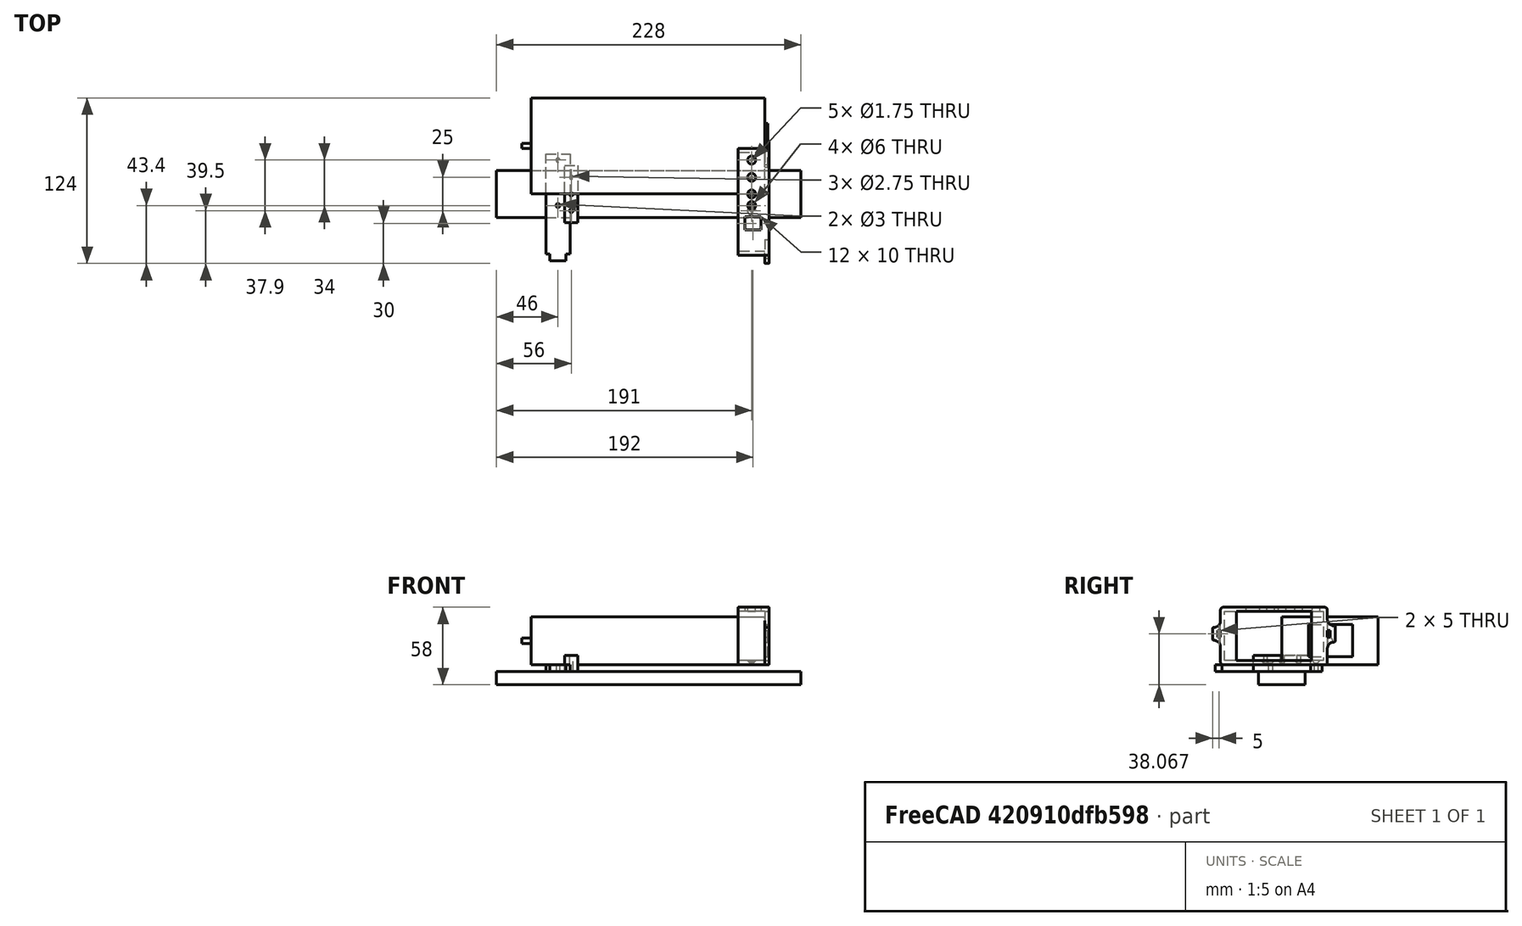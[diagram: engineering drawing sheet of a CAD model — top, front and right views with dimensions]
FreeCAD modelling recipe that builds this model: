
FCSTD DOCUMENT  (FreeCAD 0.18R)
Label: Powerbrick-Shoes
License: CreativeCommons Attribution
LicenseURL: http://creativecommons.org/licenses/by/4.0/
objects: Sketcher::SketchObject×6, Part::Box×4, PartDesign::Pad×4, PartDesign::Body×3, App::Part×2, Mesh::Feature×2, Part::Cylinder×1, Part::MultiFuse×1, PartDesign::Pocket×1, PartDesign::Hole×1, Part::Mirroring×1
note: 28 computed .brp shape members not serialized (recipe doc carries the construction recipe); baked Part::Feature solids carry a one-line shape summary decoded from their .brp

FEATURE [Part::Box] Box  label="Powerbrick-mw-gst160a"
  AttacherType = Attacher::AttachEngine3D
  Height = 36
  Length = 175
  Width = 72
FEATURE [Sketcher::SketchObject] Sketch
  MapMode = 5
  Support = -> [XY_Plane]
  sketch-geometry (10):
    g0: LineSegment StartX=-9 StartY=30 StartZ=0 EndX=9 EndY=30 EndZ=0
    g1: LineSegment StartX=9 StartY=30 StartZ=0 EndX=9 EndY=-45 EndZ=0
    g2: LineSegment StartX=-9 StartY=-45 StartZ=0 EndX=-9 EndY=30 EndZ=0
    g3: LineSegment StartX=-9 StartY=-45 StartZ=0 EndX=-6 EndY=-45 EndZ=0
    g4: LineSegment StartX=6 StartY=-45 StartZ=0 EndX=9 EndY=-45 EndZ=0
    g5: Circle CenterX=0 CenterY=25.4 CenterZ=0 NormalX=0 NormalY=0 NormalZ=1 AngleXU=0 Radius=1.5
    g6: Circle CenterX=0 CenterY=-8.6 CenterZ=0 NormalX=0 NormalY=0 NormalZ=1 AngleXU=0 Radius=1.5
    g7: LineSegment StartX=6 StartY=-45 StartZ=0 EndX=6 EndY=-50 EndZ=0
    g8: LineSegment StartX=6 StartY=-50 StartZ=0 EndX=-6 EndY=-50 EndZ=0
    g9: LineSegment StartX=-6 StartY=-50 StartZ=0 EndX=-6 EndY=-45 EndZ=0
  constraints (29):
    c: Coincident(g0,g1)
    c: Coincident(g2,g0)
    c: Vertical(g1)
    c: Vertical(g2)
    c: Coincident(g1,g4)
    c: Coincident(g2,g3)
    c: Horizontal(g3)
    c: Horizontal(g4)
    c: Equal(g2,g1)
    c: Symmetric(g0,g0,g-2)
    c: PointOnObject(g5,g-2)
    c: PointOnObject(g6,g-2)
    c: Radius(g5) = 1.5
    c: Equal(g5,g6)
    c: DistanceX(g0,g0) = 18
    c: DistanceY(g2,g2) = 75
    c: Coincident(g7,g8)
    c: Coincident(g8,g9)
    c: Coincident(g4,g7)
    c: Coincident(g9,g3)
    c: Vertical(g7)
    c: Vertical(g9)
    c: Horizontal(g8)
    c: Equal(g4,g3)
    c: DistanceX(g8,g8) = 12
    c: DistanceY(g7,g7) = 5
    c: DistanceY(g2,g-1) = 45
    c: DistanceY(g6,g-1) = 8.6
    c: DistanceY(g-1,g5) = 25.4
FEATURE [PartDesign::Pad] Pad
  Length = 5
  Length2 = 100
  Profile = -> Sketch
  Type = 0
FEATURE [PartDesign::Body] Body  label="APRA-Norm-Hutschienenklammer-442-311-35"
  Group = -> [Sketch,Pad]
  Origin = -> Origin
  Placement = pos=(20,0,-5) rot=(0,0,1;0rad)
  Tip = -> Pad
FEATURE [Part::Box] Box001  label="DIN Rail"
  AttacherType = Attacher::AttachEngine3D
  Height = 10
  Length = 228
  Placement = pos=(-26,-17.5,-15) rot=(0,0,1;0rad)
  Width = 35
FEATURE [Sketcher::SketchObject] Sketch001
  MapMode = 5
  Support = -> [XY_Plane001]
  sketch-geometry (7):
    g0: LineSegment StartX=-5 StartY=21.5 StartZ=0 EndX=5 EndY=21.5 EndZ=0
    g1: LineSegment StartX=5 StartY=21.5 StartZ=0 EndX=5 EndY=-21.5 EndZ=0
    g2: LineSegment StartX=5 StartY=-21.5 StartZ=0 EndX=-5 EndY=-21.5 EndZ=0
    g3: LineSegment StartX=-5 StartY=-21.5 StartZ=0 EndX=-5 EndY=21.5 EndZ=0
    g4: Circle CenterX=0 CenterY=12.5 CenterZ=0 NormalX=0 NormalY=0 NormalZ=1 AngleXU=0 Radius=1.375
    g5: Circle CenterX=0 CenterY=0 CenterZ=0 NormalX=0 NormalY=0 NormalZ=1 AngleXU=0 Radius=1.375
    g6: Circle CenterX=0 CenterY=-12.5 CenterZ=0 NormalX=0 NormalY=0 NormalZ=1 AngleXU=0 Radius=1.375
  constraints (17):
    c: Coincident(g0,g1)
    c: Coincident(g1,g2)
    c: Coincident(g2,g3)
    c: Coincident(g3,g0)
    c: Horizontal(g2)
    c: Vertical(g1)
    c: Symmetric(g0,g0,g-2)
    c: DistanceX(g0,g0) = 10
    c: DistanceY(g3,g3) = 43
    c: Symmetric(g2,g0,g-1)
    c: PointOnObject(g6,g-2)
    c: Coincident(g-1,g5)
    c: Symmetric(g6,g4,g-1)
    c: DistanceY(g6,g4) = 25
    c: Radius(g4) = 1.375
    c: Equal(g4,g5)
    c: Equal(g4,g6)
FEATURE [PartDesign::Pad] Pad001
  Length = 12
  Length2 = 100
  Profile = -> Sketch001
  Type = 0
FEATURE [PartDesign::Body] Body001  label="China-Clamp-DIN-Rail"
  Group = -> [Sketch001,Pad001]
  Origin = -> Origin001
  Placement = pos=(30,0,-5) rot=(0,0,1;0rad)
  Tip = -> Pad001
FEATURE [Sketcher::SketchObject] Sketch002
  MapMode = 5
  Placement = pos=(0,0,0) rot=(0.57735,0.57735,0.57735;2.0944rad)
  Support = -> [YZ_Plane003]
  sketch-geometry (12):
    g0: LineSegment StartX=-43 StartY=3 StartZ=0 EndX=-43 EndY=40 EndZ=0
    g1: LineSegment StartX=-43 StartY=40 StartZ=0 EndX=31 EndY=40 EndZ=0
    g2: LineSegment StartX=31 StartY=40 StartZ=0 EndX=31 EndY=3 EndZ=0
    g3: LineSegment StartX=31 StartY=3 StartZ=0 EndX=-43 EndY=3 EndZ=0
    g4: LineSegment StartX=-46 StartY=2 StartZ=0 EndX=-46 EndY=41 EndZ=0
    g5: ArcOfCircle CenterX=-44 CenterY=41 CenterZ=0 NormalX=0 NormalY=0 NormalZ=1 AngleXU=0 Radius=2 StartAngle=1.5708 EndAngle=3.14159
    g6: LineSegment StartX=-44 StartY=43 StartZ=0 EndX=32 EndY=43 EndZ=0
    g7: ArcOfCircle CenterX=32 CenterY=41 CenterZ=0 NormalX=0 NormalY=0 NormalZ=1 AngleXU=0 Radius=2 StartAngle=1.6e-15 EndAngle=1.5708
    g8: LineSegment StartX=34 StartY=41 StartZ=0 EndX=34 EndY=2 EndZ=0
    g9: ArcOfCircle CenterX=32 CenterY=2 CenterZ=0 NormalX=0 NormalY=0 NormalZ=1 AngleXU=0 Radius=2 StartAngle=4.71239 EndAngle=6.28319
    g10: LineSegment StartX=32 StartY=0 StartZ=0 EndX=-44 EndY=0 EndZ=0
    g11: ArcOfCircle CenterX=-44 CenterY=2 CenterZ=0 NormalX=0 NormalY=0 NormalZ=1 AngleXU=0 Radius=2 StartAngle=3.14159 EndAngle=4.71239
  constraints (32):
    c: Coincident(g0,g1)
    c: Coincident(g1,g2)
    c: Coincident(g2,g3)
    c: Coincident(g3,g0)
    c: Tangent(g4,g5) = 1.5708
    c: Tangent(g5,g6) = 1.5708
    c: Tangent(g6,g7) = 1.5708
    c: Tangent(g7,g8) = 1.5708
    c: Tangent(g8,g9) = 1.5708
    c: Horizontal(g6)
    c: Horizontal(g1)
    c: Horizontal(g3)
    c: Vertical(g8)
    c: Vertical(g0)
    c: Vertical(g2)
    c: Vertical(g4)
    c: Tangent(g4,g11) = 1.5708
    c: Tangent(g10,g11) = 1.5708
    c: Tangent(g9,g10) = 1.5708
    c: PointOnObject(g10,g-1)
    c: Horizontal(g10)
    c: DistanceY(g-1,g2) = 3
    c: DistanceX(g3,g3) = 74
    c: DistanceY(g2,g2) = 37
    c: DistanceY(g1,g6) = 3
    c: DistanceX(g1,g7) = 3
    c: DistanceX(g4,g0) = 3
    c: Radius(g7) = 2
    c: Equal(g7,g5)
    c: Equal(g7,g11)
    c: Equal(g7,g9)
    c: DistanceX(g-1,g2) = 31
FEATURE [PartDesign::Pad] Pad002
  Length = 20
  Length2 = 100
  Placement = pos=(0,0,0) rot=(0.57735,0.57735,0.57735;2.0944rad)
  Profile = -> Sketch002
  Type = 0
FEATURE [Part::Box] Box002  label="LED"
  AttacherType = Attacher::AttachEngine3D
  Height = 10
  Length = 7
  Placement = pos=(5,18,26) rot=(0,0,1;0rad)
  Width = 4
FEATURE [Part::Cylinder] Cylinder  label="24V Cable"
  Angle = 360
  AttacherType = Attacher::AttachEngine3D
  Height = 11
  Placement = pos=(-7,36,18) rot=(0,1,0;1.5708rad)
  Radius = 2
FEATURE [Part::Box] Box003  label="230VConnector"
  AttacherType = Attacher::AttachEngine3D
  Height = 24
  Length = 10
  Placement = pos=(167,20,6) rot=(0,0,1;0rad)
  Width = 33
FEATURE [Part::MultiFuse] Fusion
  Shapes = -> [Box003,Cylinder,Box,Box002]
FEATURE [App::Part] Part001  label="GST160"
  Group = -> [Box002,Box,Cylinder,Box003,Fusion]
  Origin = -> Origin004
  Placement = pos=(0,-42,3) rot=(0,0,1;0rad)
FEATURE [Sketcher::SketchObject] CopySketch003
  Placement = pos=(0,0,0) rot=(0.57735,0.57735,0.57735;2.0944rad)
  sketch-geometry (35):
    g0: ArcOfCircle CenterX=-44 CenterY=41 CenterZ=0 NormalX=0 NormalY=0 NormalZ=1 AngleXU=0 Radius=2 StartAngle=1.5708 EndAngle=3.14159
    g1: LineSegment StartX=-6 StartY=43 StartZ=0 EndX=32 EndY=43 EndZ=0
    g2: ArcOfCircle CenterX=32 CenterY=41 CenterZ=0 NormalX=0 NormalY=0 NormalZ=1 AngleXU=0 Radius=2 StartAngle=1.4e-15 EndAngle=1.5708
    g3: ArcOfCircle CenterX=32 CenterY=2 CenterZ=0 NormalX=0 NormalY=0 NormalZ=1 AngleXU=0 Radius=2 StartAngle=4.71239 EndAngle=6.28319
    g4: LineSegment StartX=32 StartY=0 StartZ=0 EndX=-6.00286 EndY=0 EndZ=0
    g5: LineSegment StartX=-44 StartY=43 StartZ=0 EndX=-6 EndY=43 EndZ=0
    g6: ArcOfCircle CenterX=-44.0057 CenterY=2 CenterZ=0 NormalX=0 NormalY=0 NormalZ=1 AngleXU=0 Radius=2 StartAngle=3.14159 EndAngle=4.71239
    g7: LineSegment StartX=-44.0057 StartY=0 StartZ=0 EndX=-6.00286 EndY=0 EndZ=0
    g8: LineSegment StartX=-46 StartY=41 StartZ=0 EndX=-46 EndY=32.8632 EndZ=0
    g9: ArcOfCircle CenterX=-51 CenterY=32.8632 CenterZ=0 NormalX=0 NormalY=0 NormalZ=1 AngleXU=0 Radius=5 StartAngle=4.71239 EndAngle=6.28319
    g10: ArcOfCircle CenterX=-51.0057 CenterY=13.2711 CenterZ=0 NormalX=0 NormalY=0 NormalZ=1 AngleXU=0 Radius=5 StartAngle=2e-16 EndAngle=1.56984
    g11: LineSegment StartX=-46.0057 StartY=13.2711 StartZ=0 EndX=-46.0057 EndY=2 EndZ=0
    g12: LineSegment StartX=34 StartY=41 StartZ=0 EndX=34 EndY=34.1757 EndZ=0
    g13: ArcOfCircle CenterX=39 CenterY=34.1757 CenterZ=0 NormalX=0 NormalY=0 NormalZ=1 AngleXU=0 Radius=5 StartAngle=3.14159 EndAngle=4.71239
    g14: ArcOfCircle CenterX=39 CenterY=11.9585 CenterZ=0 NormalX=0 NormalY=0 NormalZ=1 AngleXU=0 Radius=5 StartAngle=1.5708 EndAngle=3.14159
    g15: LineSegment StartX=34 StartY=11.9585 StartZ=0 EndX=34 EndY=2 EndZ=0
    g16: LineSegment StartX=-46 StartY=25.5671 StartZ=0 EndX=-46 EndY=20.5671 EndZ=0
    g17: LineSegment StartX=-46 StartY=20.5671 StartZ=0 EndX=-48 EndY=20.5671 EndZ=0
    g18: LineSegment StartX=-48 StartY=20.5671 StartZ=0 EndX=-48 EndY=25.5671 EndZ=0
    g19: LineSegment StartX=34 StartY=25.5671 StartZ=0 EndX=36 EndY=25.5671 EndZ=0
    g20: LineSegment StartX=36 StartY=25.5671 StartZ=0 EndX=36 EndY=20.5671 EndZ=0
    g21: LineSegment StartX=36 StartY=20.5671 StartZ=0 EndX=34 EndY=20.5671 EndZ=0
    g22: LineSegment StartX=34 StartY=20.5671 StartZ=0 EndX=34 EndY=25.5671 EndZ=0
    g23: ArcOfCircle CenterX=-51 CenterY=26.8632 CenterZ=0 NormalX=0 NormalY=0 NormalZ=1 AngleXU=0 Radius=1 StartAngle=1.5708 EndAngle=3.14159
    g24: ArcOfCircle CenterX=-51 CenterY=19.2711 CenterZ=0 NormalX=0 NormalY=0 NormalZ=1 AngleXU=0 Radius=1 StartAngle=3.14159 EndAngle=4.71144
    g25: LineSegment StartX=-52 StartY=26.8632 StartZ=0 EndX=-52 EndY=19.2711 EndZ=0
    g26: ArcOfCircle CenterX=39 CenterY=28.1757 CenterZ=0 NormalX=0 NormalY=0 NormalZ=1 AngleXU=0 Radius=1 StartAngle=1.4e-15 EndAngle=1.5708
    g27: ArcOfCircle CenterX=39 CenterY=17.9585 CenterZ=0 NormalX=0 NormalY=0 NormalZ=1 AngleXU=0 Radius=1 StartAngle=4.71239 EndAngle=6.28319
    g28: LineSegment StartX=40 StartY=28.1757 StartZ=0 EndX=40 EndY=17.9585 EndZ=0
    g29: LineSegment [constr] StartX=-56.2805 StartY=23.0671 StartZ=0 EndX=54.5786 EndY=23.0671 EndZ=0
    g30: LineSegment StartX=-48 StartY=25.5671 StartZ=0 EndX=-46 EndY=25.5671 EndZ=0
    g31: LineSegment StartX=-34 StartY=40 StartZ=0 EndX=22 EndY=40 EndZ=0
    g32: LineSegment StartX=22 StartY=40 StartZ=0 EndX=22 EndY=3 EndZ=0
    g33: LineSegment StartX=22 StartY=3 StartZ=0 EndX=-34 EndY=3 EndZ=0
    g34: LineSegment StartX=-34 StartY=3 StartZ=0 EndX=-34 EndY=40 EndZ=0
  constraints (87):
    c: Tangent(g1,g2) = 1.5708
    c: Horizontal(g1)
    c: Tangent(g3,g4) = 1.5708
    c: Horizontal(g4)
    c: Radius(g2) = 2
    c: Equal(g2,g0)
    c: Equal(g2,g3)
    c: Tangent(g0,g5) = 1.5708
    c: Horizontal(g5)
    c: Tangent(g6,g7) = -1.5708
    c: Equal(g6,g0)
    c: Horizontal(g7)
    c: DistanceY(g3,g1) = 43
    c: PointOnObject(g7,g-1)
    c: Equal(g7,g4)
    c: Tangent(g8,g9) = 1.5708
    c: Tangent(g10,g11) = 1.5708
    c: Vertical(g11)
    c: Tangent(g6,g11) = -1.5708
    c: Tangent(g0,g8) = -1.5708
    c: Vertical(g8)
    c: Tangent(g12,g13) = -1.5708
    c: Tangent(g14,g15) = -1.5708
    c: Vertical(g15)
    c: Vertical(g12)
    c: Tangent(g3,g15) = 1.5708
    c: Tangent(g2,g12) = 1.5708
    c: DistanceX(g0,g2) = 80
    c: Equal(g5,g1)
    c: DistanceX(g-1,g2) = 34
    c: Coincident(g16,g17)
    c: Coincident(g17,g18)
    c: Horizontal(g17)
    c: Vertical(g16)
    c: Vertical(g18)
    c: Coincident(g19,g20)
    c: Coincident(g20,g21)
    c: Coincident(g21,g22)
    c: Coincident(g22,g19)
    c: Horizontal(g19)
    c: Horizontal(g21)
    c: Vertical(g20)
    c: Vertical(g12,g19)
    c: DistanceX(g17,g17) = 2
    c: DistanceY(g16,g16) = 5
    c: Equal(g22,g16)
    c: Tangent(g24,g25) = -1.5708
    c: Tangent(g23,g25) = -1.5708
    c: Tangent(g23,g9) = 1.5708
    c: Tangent(g10,g24) = 1.5708
    c: Tangent(g27,g28) = 1.5708
    c: Tangent(g26,g28) = 1.5708
    c: Tangent(g13,g26) = 1.5708
    c: Tangent(g14,g27) = 1.5708
    c: Radius(g27) = 1
    c: Equal(g27,g26)
    c: Equal(g27,g23)
    c: Equal(g27,g24)
    c: Vertical(g12,g14)
    c: Radius(g13) = 5
    c: Equal(g13,g14)
    c: Equal(g13,g9)
    c: Equal(g13,g10)
    c: DistanceX(g2,g26) = 6
    c: DistanceX(g23,g0) = 6
    c: Symmetric(g16,g16,g29)
    c: Symmetric(g23,g24,g29)
    c: Symmetric(g19,g21,g29)
    c: Symmetric(g26,g27,g29)
    c: Equal(g17,g21)
    c: Horizontal(g30)
    c: Coincident(g16,g30)
    c: Coincident(g18,g30)
    c: Coincident(g31,g32)
    c: Coincident(g32,g33)
    c: Coincident(g33,g34)
    c: Coincident(g34,g31)
    c: Horizontal(g31)
    c: Horizontal(g33)
    c: Vertical(g32)
    c: Vertical(g34)
    c: Coincident(g5,g1)
    c: Coincident(g7,g4)
    c: DistanceY(g31,g0) = 3
    c: DistanceY(g3,g32) = 3
    c: DistanceX(g31,g1) = 10
    c: DistanceX(g0,g31) = 10
FEATURE [PartDesign::Pad] Pad003
  BaseFeature = -> Pad002
  Length = 3
  Length2 = 100
  Placement = pos=(0,0,0) rot=(0.57735,0.57735,0.57735;2.0944rad)
  Profile = -> CopySketch003
  Reversed = true
  Type = 0
FEATURE [Sketcher::SketchObject] Sketch003
  MapMode = 5
  Placement = pos=(-1.2e-14,1.89e-14,43) rot=(0,0,-1;1.5708rad)
  Support = -> [Pad003]
  sketch-geometry (8):
    g0: Circle CenterX=-25.4 CenterY=10 CenterZ=0 NormalX=0 NormalY=0 NormalZ=1 AngleXU=0 Radius=3
    g1: Circle CenterX=8.6 CenterY=10 CenterZ=0 NormalX=0 NormalY=0 NormalZ=1 AngleXU=0 Radius=3
    g2: LineSegment StartX=17 StartY=15 StartZ=0 EndX=27 EndY=15 EndZ=0
    g3: LineSegment StartX=27 StartY=15 StartZ=0 EndX=27 EndY=3 EndZ=0
    g4: LineSegment StartX=27 StartY=3 StartZ=0 EndX=17 EndY=3 EndZ=0
    g5: LineSegment StartX=17 StartY=3 StartZ=0 EndX=17 EndY=15 EndZ=0
    g6: Circle CenterX=0 CenterY=10 CenterZ=0 NormalX=0 NormalY=0 NormalZ=1 AngleXU=0 Radius=3
    g7: Circle CenterX=-12.5 CenterY=10 CenterZ=0 NormalX=0 NormalY=0 NormalZ=1 AngleXU=0 Radius=3
  constraints (24):
    c: Coincident(g2,g3)
    c: Coincident(g3,g4)
    c: Coincident(g4,g5)
    c: Coincident(g5,g2)
    c: Horizontal(g2)
    c: Horizontal(g4)
    c: Vertical(g3)
    c: Vertical(g5)
    c: DistanceX(g-1,g1) = 8.6
    c: DistanceX(g0,g-1) = 25.4
    c: Horizontal(g0,g1)
    c: DistanceY(g-1,g1) = 10
    c: DistanceX(g2,g2) = 10
    c: DistanceY(g3,g3) = 12
    c: DistanceX(g-1,g4) = 17
    c: DistanceY(g-1,g4) = 3
    c: Radius(g0) = 3
    c: Equal(g0,g1)
    c: Horizontal(g0,g7)
    c: Horizontal(g7,g6)
    c: Equal(g0,g7)
    c: Equal(g7,g6)
    c: PointOnObject(g6,g-2)
    c: DistanceX(g7,g-1) = 12.5
FEATURE [PartDesign::Pocket] Pocket
  BaseFeature = -> Pad003
  Length = 5
  Length2 = 100
  Placement = pos=(0,0,0) rot=(0.57735,0.57735,0.57735;2.0944rad)
  Profile = -> Sketch003
  Type = 0
FEATURE [Sketcher::SketchObject] Sketch004
  MapMode = 5
  Placement = pos=(-8e-16,1.7e-15,3) rot=(0,0,-1;1.5708rad)
  Support = -> [Pocket]
  sketch-geometry (5):
    g0: Circle CenterX=-25.4 CenterY=10 CenterZ=0 NormalX=0 NormalY=0 NormalZ=1 AngleXU=0 Radius=1.5
    g1: Circle CenterX=8.6 CenterY=10 CenterZ=0 NormalX=0 NormalY=0 NormalZ=1 AngleXU=0 Radius=1.5
    g2: Circle CenterX=-12.5 CenterY=10 CenterZ=0 NormalX=0 NormalY=0 NormalZ=1 AngleXU=0 Radius=1.5
    g3: Circle CenterX=0 CenterY=10 CenterZ=0 NormalX=0 NormalY=0 NormalZ=1 AngleXU=0 Radius=1.5
    g4: Circle CenterX=12.5 CenterY=10 CenterZ=0 NormalX=0 NormalY=0 NormalZ=1 AngleXU=0 Radius=1.5
  constraints (14):
    c: Horizontal(g0,g1)
    c: DistanceY(g-1,g0) = 10
    c: Radius(g0) = 1.5
    c: Equal(g0,g1)
    c: DistanceX(g0,g-1) = 25.4
    c: DistanceX(g-1,g1) = 8.6
    c: Horizontal(g0,g2)
    c: Horizontal(g2,g3)
    c: Equal(g0,g2)
    c: Equal(g2,g3)
    c: Equal(g1,g4)
    c: PointOnObject(g3,g-2)
    c: Symmetric(g2,g4,g-2)
    c: DistanceX(g2,g4) = 25
FEATURE [PartDesign::Hole] Hole
  BaseFeature = -> Pocket
  Depth = 5
  DepthType = 0
  Diameter = 1.75
  DrillPoint = 1
  DrillPointAngle = 118
  HoleCutCountersinkAngle = 90
  HoleCutDepth = 2
  HoleCutDiameter = 6.2
  HoleCutType = 2
  ModelActualThread = false
  Placement = pos=(0,0,0) rot=(0.57735,0.57735,0.57735;2.0944rad)
  Profile = -> Sketch004
  Tapered = false
  TaperedAngle = 90
  ThreadAngle = 0
  ThreadClass = 0
  ThreadCutOffInner = 0
  ThreadCutOffOuter = 0
  ThreadDirection = 0
  ThreadFit = 0
  ThreadPitch = 0
  ThreadSize = 0
  ThreadType = 0
  Threaded = false
FEATURE [PartDesign::Body] Body002  label="BracketLeft"
  Group = -> [Sketch002,Pad002,Pad003,Sketch003,Pocket,Sketch004,Hole]
  Origin = -> Origin003
  Tip = -> Hole
FEATURE [Part::Mirroring] Part__Mirroring  label="BracketRight"
  Base = (0,0,0)
  Normal = (1,0,0)
  Placement = pos=(175,0,0) rot=(0,0,1;0rad)
  Source = -> Body002
FEATURE [App::Part] Part  label="Powerbrick Shoes GST160"
  Group = -> [Body002,CopySketch003,Part__Mirroring]
  Origin = -> Origin002
FEATURE [Mesh::Feature] Mesh  label="BracketLeft (Meshed)"
  Placement = pos=(0,0,0) rot=(0,1,0;4.71239rad)
FEATURE [Mesh::Feature] Mesh001  label="BracketRight (Meshed)"
  Placement = pos=(38,0,174) rot=(0,1,0;1.5708rad)
